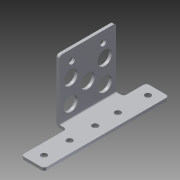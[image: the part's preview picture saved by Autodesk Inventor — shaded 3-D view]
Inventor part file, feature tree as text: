
AUTODESK INVENTOR PART (.ipt)
format: ipt  version: 2014 SP1 (Build 180222100, 222)  size: 251,392 bytes
history: native  units: in
note: dims shown in document units (in); Inventor stores cm internally (conversion verified against a paired STEP export)
features: other x4, sheet_metal_op x3, sketch x3, chamfer x1, reference x1
ambient origin geometry x8: Origin, YZ Plane, XZ Plane, XY Plane, X Axis, Y Axis, Z Axis, Center Point
bodies: Solid1 (feature_tree)
feature tree (12):
  sheet_metal_op  "Face1"
  sheet_metal_op  "Flange1"
  chamfer  "Corner Round1"
  sketch  "Sketch1"  dims[d0=1.0in]
  other  "Plate1"
  sketch  "Sketch2"  dims[d1=5.5in]
  other  "Plate2"
  sheet_metal_op  "Bend1"
  sketch  "Sketch3"  dims[d2=0.5in d3=1.125in d4=1.125in d5=1.0in d6=1.325in d7=0.26in d8=2.5in d9=0.454in d10=2.0in d11=0.125in d12=0.125in d13=0.0625in d14=0.25in d15=0.125in d16=2.75in d17=90.0deg d18=0.05in d19=0.5in d20=0.125in d21=0.125in d22=0.125in d23=0.266in d25=0.266in d26=0.125in d27=0.0in d28=0.625in d29=0.7874in d31=1.0in d32=0.7874in d34=1.5in d37=0.5in d38=0.625in]
  reference  "Reference1"
  other  "Cut1"
  other  "Definition1"
